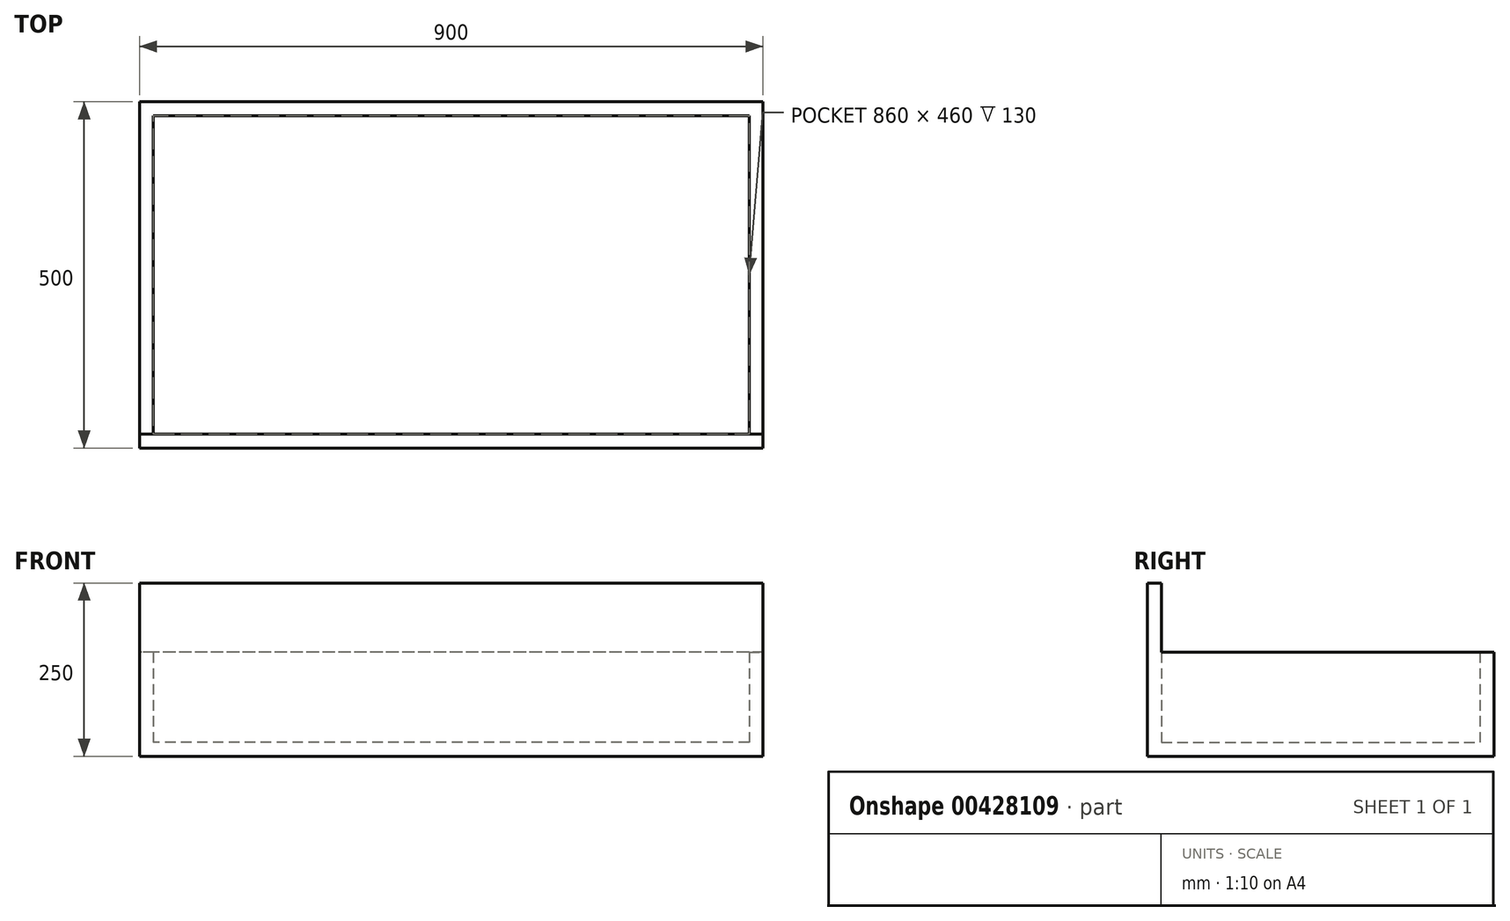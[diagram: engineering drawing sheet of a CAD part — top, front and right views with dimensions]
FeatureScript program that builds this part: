
annotation { "Feature Type Name" : "Feature", "Feature Type Description" : "" }
export const myFeature = defineFeature(function(context is Context, id is Id, definition is map)
    precondition{}
    {
        {
            var Q0;
            Q0=qCreatedBy(makeId("Top.planeOp"),FACE);
            var sketch = newSketch(context, id + "F0", { "sketchPlane" : qUnion([Q0])});
            skLineSegment(sketch, "E0.bottom", {"start": v(450, -250) * mm, "end": v(-450, -250) * mm});
            skLineSegment(sketch, "E0.top", {"start": v(450, 250) * mm, "end": v(-450, 250) * mm});
            skLineSegment(sketch, "E0.left", {"start": v(450, -250) * mm, "end": v(450, 230) * mm});
            skLineSegment(sketch, "E0.right", {"start": v(-450, -250) * mm, "end": v(-450, 250) * mm});
            skPoint(sketch, "E0.middle", {"position": v(0, 0) * mm});
            skLineSegment(sketch, "E1.0", {"start": v(430, -230) * mm, "end": v(-430, -230) * mm});
            skLineSegment(sketch, "E2.0", {"start": v(430, -230) * mm, "end": v(430, 230) * mm});
            skLineSegment(sketch, "E3.0", {"start": v(430, 230) * mm, "end": v(-430, 230) * mm});
            skLineSegment(sketch, "E4.0", {"start": v(-430, -230) * mm, "end": v(-430, 230) * mm});
            skLineSegment(sketch, "E5", {"start": v(450, 230) * mm, "end": v(450, 250) * mm});
            skLineSegment(sketch, "E6", {"start": v(430, -230) * mm, "end": v(450, -230) * mm});
            skLineSegment(sketch, "E7", {"start": v(-430, -230) * mm, "end": v(-450, -230) * mm});
            skSolve(sketch);
        }
        {
            var Q0;
            {var subQ1=sQuery(id+"F0.wireOp",EDGE,"E0.top");Q0=makeQuery(id+"F0.imprint","IMPRINT",FACE,{"disambiguationData":[TD([[makeQuery(id+"F0.imprint","IMPRINT",EDGE,{"derivedFrom":subQ1}),1.0]])]});}
            extrude(context, id + "F1", {"entities" : qUnion([Q0]), "depth" : 150 * mm});
        }
        {
            var Q0;
            Q0 = qSketchRegion(id + "F0", true);
            var Q1;
            Q1=makeQuery(id+"F0.imprint","IMPRINT",FACE,{"disambiguationData":[TD([[makeQuery(id+"F0.imprint","IMPRINT",EDGE,{"derivedFrom":sQuery(id+"F0.wireOp",EDGE,"E1.0")}),-1.0]])]});
            extrude(context, id + "F2", {"entities" : qUnion([Q0, Q1]), "operationType" : NewBodyOperationType.ADD, "depth" : 20 * mm});
        }
        {
            var Q0;
            {var subQ1=sQuery(id+"F0.wireOp",EDGE,"E0.bottom");Q0=makeQuery(id+"F0.imprint","IMPRINT",FACE,{"disambiguationData":[TD([[makeQuery(id+"F0.imprint","IMPRINT",EDGE,{"derivedFrom":subQ1}),-1.0]])]});}
            extrude(context, id + "F3", {"entities" : qUnion([Q0]), "operationType" : NewBodyOperationType.ADD, "depth" : 250 * mm});
        }
    });
